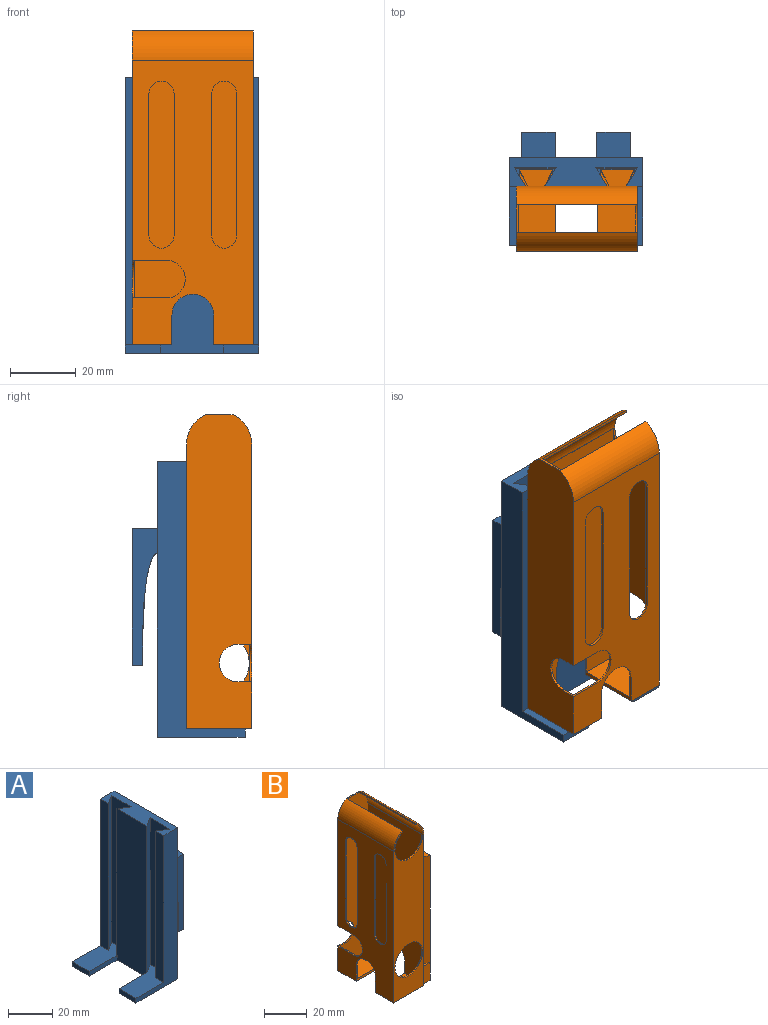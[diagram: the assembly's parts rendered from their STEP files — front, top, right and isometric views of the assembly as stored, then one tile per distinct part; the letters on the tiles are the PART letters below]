
ASSEMBLY  parts=2 mates=1
PART A: 34 faces, bbox 34.3x40.6x83.8 mm
  f0: plane 40.64x26.67mm, normal (0,0,-1), area 745.2mm2, adj f2,f5,f9,f18,f19,f20,f32,f33
  f1: plane 23.37x14.29mm, normal (0,0,1), area 243mm2, adj f2,f3,f9,f14,f15,f16,f20,f33
  f2: plane 10.8x2.54mm, normal (-1,0,0), area 27.4mm2, adj f0,f1,f20,f33
  f3: plane 81.28x5.14mm, normal (-1,0,0), area 418.1mm2, adj f1,f4,f14,f33
  f4: plane 40.64x8.89mm, normal (0,0,1), area 259.1mm2, adj f3,f5,f9,f10,f11,f12,f13,f14
  f5: plane 83.82x40.64mm, normal (1,0,0), area 3251.7mm2, adj f0,f4,f6,f7,f8,f21,f22,f24
  f6: plane 41.59x7.62mm, normal (0,1,0), area 190.3mm2, adj f5,f21,f23,f29,f30,f31
  f7: plane 41.59x7.62mm, normal (0,-1,0), area 190.3mm2, adj f5,f24,f25,f26,f27,f28
  f8: plane 41.59x7.62mm, normal (0,1,0), area 190.3mm2, adj f5,f24,f25,f26,f27,f28
  f9: plane 83.82x19.18mm, normal (-1,0,0), area 1607.1mm2, adj f0,f1,f4,f13,f15,f17,f19,f20
  f10: plane 81.28x5.14mm, normal (-1,0,0), area 418.1mm2, adj f4,f11,f17,f32
  f11: plane 81.28x5.59mm, normal (0.54,0.84,0), area 538.4mm2, adj f4,f10,f12,f17
  f12: plane 81.28x12.7mm, normal (-1,0,0), area 1032.3mm2, adj f4,f11,f13,f17
  f13: plane 81.28x5.59mm, normal (0.54,-0.84,0), area 538.4mm2, adj f4,f9,f12,f17
  f14: plane 81.28x5.59mm, normal (0.54,-0.84,0), area 538.4mm2, adj f1,f3,f4,f16
  f15: plane 81.28x5.59mm, normal (0.54,0.84,0), area 538.4mm2, adj f1,f4,f9,f16
  f16: plane 81.28x12.7mm, normal (-1,0,0), area 1032.3mm2, adj f1,f4,f14,f15
  f17: plane 23.37x14.29mm, normal (0,0,1), area 243mm2, adj f9,f10,f11,f12,f13,f18,f19,f32
  f18: plane 10.8x2.54mm, normal (-1,0,0), area 27.4mm2, adj f0,f17,f19,f32
  f19: plane 17.78x2.54mm, normal (0,1,0), area 45.2mm2, adj f0,f9,f17,f18
  f20: plane 17.78x2.54mm, normal (0,-1,0), area 45.2mm2, adj f0,f1,f2,f9
  f21: plane 10.16x7.62mm, normal (0,0,1), area 77.4mm2, adj f5,f6,f22,f23
  f22: plane 41.59x7.62mm, normal (0,-1,0), area 190.3mm2, adj f5,f21,f23,f29,f30,f31
  f23: plane 41.59x10.16mm, normal (1,0,0), area 422.6mm2, adj f6,f21,f22,f29
  f24: plane 10.16x7.62mm, normal (0,0,1), area 77.4mm2, adj f5,f7,f8,f25
  f25: plane 41.59x10.16mm, normal (1,0,0), area 422.6mm2, adj f7,f8,f24,f28
  f26: extruded ~24.13x10.16mm, area 255.8mm2, adj f5,f7,f8,f27
  f27: plane 10.16x9.84mm, normal (-1,0,0), area 100mm2, adj f7,f8,f26,f28
  f28: plane 10.16x3.22mm, normal (0,0,-1), area 32.7mm2, adj f7,f8,f25,f27
  f29: plane 10.16x3.22mm, normal (0,0,-1), area 32.7mm2, adj f6,f22,f23,f30
  f30: plane 10.16x9.84mm, normal (-1,0,0), area 100mm2, adj f6,f22,f29,f31
  f31: extruded ~24.13x10.16mm, area 255.8mm2, adj f5,f6,f22,f30
  f32: plane 83.82x26.67mm, normal (0,-1,0), area 790.3mm2, adj f0,f4,f5,f10,f17,f18
  f33: plane 83.82x26.67mm, normal (0,1,0), area 790.3mm2, adj f0,f1,f2,f3,f4,f5
PART B: 53 faces, bbox 24.9x36.8x95.3 mm
  f0: plane 86.36x36.83mm, normal (-1,0,0), area 2084.8mm2, adj f6,f7,f16,f17,f22,f24,f25,f26
  f1: plane 10.16x5.08mm, normal (0,-1,0), area 51.6mm2, adj f5,f7,f41,f49
  f2: plane 10.16x5.08mm, normal (0,1,0), area 51.6mm2, adj f5,f7,f41,f51
  f3: plane 10.16x5.08mm, normal (0,-1,0), area 51.6mm2, adj f5,f17,f43,f45
  f4: plane 10.16x5.08mm, normal (0,1,0), area 51.6mm2, adj f5,f17,f43,f47
  f5: plane 86.36x36.83mm, normal (1,0,0), area 2178.6mm2, adj f1,f2,f3,f4,f6,f7,f16,f17
  f6: plane 95.32x19.81mm, normal (0,1,0), area 1760.5mm2, adj f0,f5,f17,f19,f22,f23,f35,f36
  f7: plane 24.89x12.07mm, normal (0,0,-1), area 290.6mm2, adj f0,f1,f2,f5,f16,f34,f41
  f8: plane 85.09x35.56mm, normal (-1,0,0), area 2865.7mm2, adj f10,f14,f15,f18,f20,f33,f34,f39
  f9: plane 85.09x35.56mm, normal (1,0,0), area 1953.3mm2, adj f10,f14,f15,f18,f21,f24,f25,f26
  f10: plane 18.54x11.43mm, normal (0,0,1), area 211.9mm2, adj f8,f9,f14,f33
  f11: plane 36.2x0.85mm, normal (-1,0,0), area 30.8mm2, adj f12,f14,f16,f19
  f12: cylinder r=9.14mm len=36.2mm, axis (0,-1,0), area 740.5mm2, adj f11,f13,f14,f15,f16,f20,f21
  f13: plane 36.2x0.85mm, normal (1,0,0), area 30.8mm2, adj f12,f14,f16,f22
  f14: plane 94.05x18.54mm, normal (0,-1,0), area 1618.4mm2, adj f8,f9,f10,f11,f12,f13,f20,f21
  f15: plane 85.09x18.54mm, normal (0,1,0), area 1183.7mm2, adj f8,f9,f12,f18,f20,f21,f32
  f16: plane 95.32x19.81mm, normal (0,-1,0), area 1333.1mm2, adj f0,f5,f7,f11,f12,f13,f19,f22
  f17: plane 24.89x12.07mm, normal (0,0,-1), area 290.6mm2, adj f0,f3,f4,f5,f6,f33,f43
  f18: plane 18.54x11.43mm, normal (0,0,1), area 211.9mm2, adj f8,f9,f15,f34
  f19: cylinder r=9.91mm len=36.83mm, axis (0,-1,0), area 412.5mm2, adj f5,f6,f11,f16,f23
  f20: plane 35.56x0.13mm, normal (0,0,-1), area 4.5mm2, adj f8,f12,f14,f15
  f21: plane 35.56x0.13mm, normal (0,0,-1), area 4.5mm2, adj f9,f12,f14,f15
  f22: cylinder r=9.91mm len=36.83mm, axis (0,-1,0), area 412.5mm2, adj f0,f6,f13,f16,f23
  f23: plane 8.44x0.64mm, normal (0,0,1), area 5.4mm2, adj f6,f14,f19,f22
  f24: cylinder r=3.81mm len=7.62mm, axis (-1,0,0), area 7.6mm2, adj f0,f9,f25,f27
  f25: plane 43.18x0.64mm, normal (0,1,0), area 27.4mm2, adj f0,f9,f24,f26
  f26: cylinder r=3.81mm len=7.62mm, axis (-1,0,0), area 7.6mm2, adj f0,f9,f25,f27
  f27: plane 43.18x0.64mm, normal (0,-1,0), area 27.4mm2, adj f0,f9,f24,f26
  f28: cylinder r=3.81mm len=7.62mm, axis (-1,0,0), area 7.6mm2, adj f0,f9,f29,f31
  f29: plane 43.18x0.64mm, normal (0,1,0), area 27.4mm2, adj f0,f9,f28,f30
  f30: cylinder r=3.81mm len=7.62mm, axis (-1,0,0), area 7.6mm2, adj f0,f9,f29,f31
  f31: plane 43.18x0.64mm, normal (0,-1,0), area 27.4mm2, adj f0,f9,f28,f30
  f32: cylinder r=9.14mm len=18.29mm, axis (0,-1,0), area 36.5mm2, adj f15,f16
  f33: plane 19.81x8.89mm, normal (0,-1,0), area 34.8mm2, adj f0,f5,f8,f9,f10,f17,f38,f39
  f34: plane 19.81x8.89mm, normal (0,1,0), area 34.8mm2, adj f0,f5,f7,f8,f9,f18,f38,f39
  f35: plane 10.41x4.19mm, normal (0,0,-1), area 8.9mm2, adj f0,f6,f9,f14,f36,f52
  f36: cylinder r=5.71mm len=11.43mm, axis (0,1,0), area 11.4mm2, adj f6,f14,f35,f37
  f37: plane 10.41x4.19mm, normal (0,0,1), area 8.9mm2, adj f0,f6,f9,f14,f36,f52
  f38: cylinder r=6.35mm len=12.7mm, axis (1,0,0), area 12.7mm2, adj f0,f9,f33,f34
  f39: cylinder r=6.35mm len=12.7mm, axis (1,0,0), area 12.7mm2, adj f5,f8,f33,f34
  f40: plane 10.16x5.08mm, normal (0,0,1), area 38.7mm2, adj f5,f41,f48,f50
  f41: plane 71.12x10.16mm, normal (1,0,0), area 722.6mm2, adj f1,f2,f7,f40,f48,f50
  f42: plane 10.16x5.08mm, normal (0,0,1), area 38.7mm2, adj f5,f43,f44,f46
  f43: plane 71.12x10.16mm, normal (1,0,0), area 722.6mm2, adj f3,f4,f17,f42,f44,f46
  f44: plane 60.96x5.08mm, normal (-0.45,-0.89,0), area 346.2mm2, adj f5,f42,f43,f45
  f45: plane 5.08x2.54mm, normal (0,0,1), area 6.5mm2, adj f3,f5,f44
  f46: plane 60.96x5.08mm, normal (-0.45,0.89,0), area 346.2mm2, adj f5,f42,f43,f47
  f47: plane 5.08x2.54mm, normal (0,0,1), area 6.5mm2, adj f4,f5,f46
  f48: plane 60.96x5.08mm, normal (-0.45,-0.89,0), area 346.2mm2, adj f5,f40,f41,f49
  f49: plane 5.08x2.54mm, normal (0,0,1), area 6.5mm2, adj f1,f5,f48
  f50: plane 60.96x5.08mm, normal (-0.45,0.89,0), area 346.2mm2, adj f5,f40,f41,f51
  f51: plane 5.08x2.54mm, normal (0,0,1), area 6.5mm2, adj f2,f5,f50
  f52: cylinder r=5.71mm len=11.43mm, axis (-1,0,0), area 11.4mm2, adj f0,f9,f35,f37
PLACE A rot(axis=(0,0,1),90deg) t=(-55.04,-17.59,12.38)mm fixed
PLACE B rot(axis=(0,0,1),90deg) t=(-54.78,-36.38,12.58)mm
MATE slider B.f40 <-> A.f4  axis (0,0,1) through (-39.86,-26.48,83.7)mm
